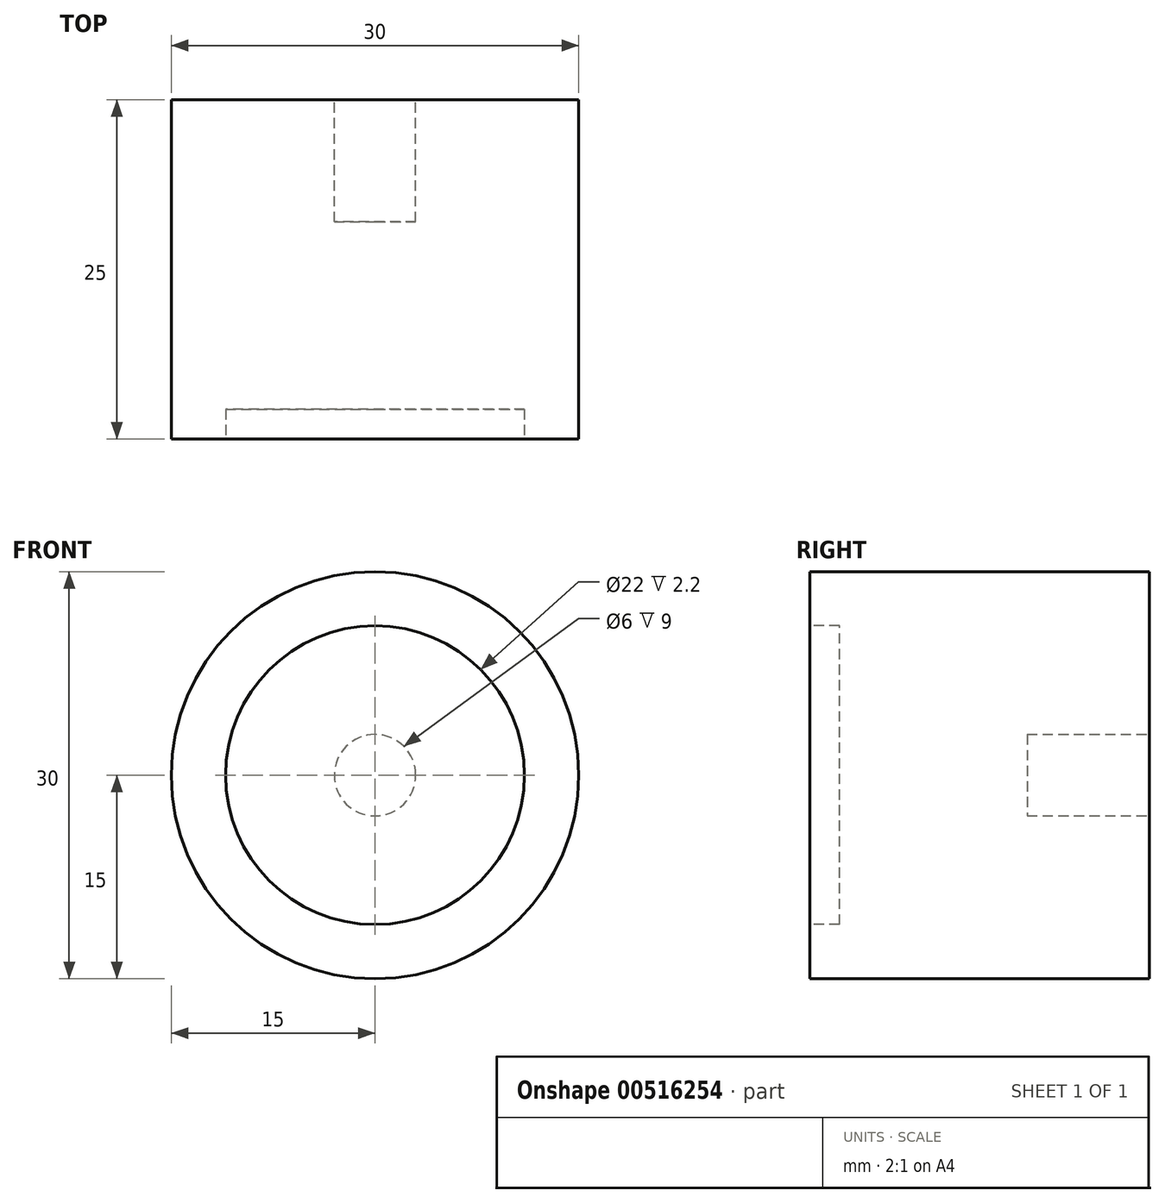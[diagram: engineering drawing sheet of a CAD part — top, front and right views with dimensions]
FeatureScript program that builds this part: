
annotation { "Feature Type Name" : "Feature", "Feature Type Description" : "" }
export const myFeature = defineFeature(function(context is Context, id is Id, definition is map)
    precondition{}
    {
        {
            var Q0;
            Q0=qCreatedBy(makeId("Front.planeOp"),FACE);
            var sketch = newSketch(context, id + "F0", { "sketchPlane" : qUnion([Q0])});
            skCircle(sketch, "E0", {"center": v(0, 0) * mm, "radius": 15 * mm});
            skSolve(sketch);
        }
        {
            var Q0;
            Q0 = qSketchRegion(id + "F0", true);
            extrude(context, id + "F1", {"entities" : qUnion([Q0]), "depth" : 25 * mm, "offsetDistance" : 25 * mm});
        }
        {
            var Q0;
            Q0=makeQuery(id+"F1.opExtrude","CAP_FACE",FACE,{"disambiguationData":[OSD([sQuery(id+"F0.wireOp",EDGE,"E0")])],"isStart":false});
            var sketch = newSketch(context, id + "F2", { "sketchPlane" : qUnion([Q0])});
            skCircle(sketch, "E1", {"center": v(0, 0) * mm, "radius": 11 * mm});
            skSolve(sketch);
        }
        {
            var Q0;
            Q0 = qSketchRegion(id + "F2", true);
            extrude(context, id + "F3", {"entities" : qUnion([Q0]), "operationType" : NewBodyOperationType.REMOVE, "oppositeDirection" : true, "depth" : 2.2 * mm, "offsetDistance" : 25 * mm});
        }
        {
            var Q0;
            Q0=makeQuery(id+"F1.opExtrude","CAP_FACE",FACE,{"disambiguationData":[OSD([sQuery(id+"F0.wireOp",EDGE,"E0")])],"isStart":true});
            var sketch = newSketch(context, id + "F4", { "sketchPlane" : qUnion([Q0])});
            skCircle(sketch, "E2", {"center": v(0, 0) * mm, "radius": 3 * mm});
            skSolve(sketch);
        }
        {
            var Q0;
            Q0 = qSketchRegion(id + "F4", true);
            extrude(context, id + "F5", {"entities" : qUnion([Q0]), "operationType" : NewBodyOperationType.REMOVE, "oppositeDirection" : true, "depth" : 9 * mm, "offsetDistance" : 25 * mm});
        }
    });
